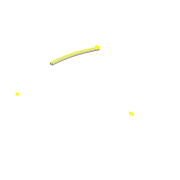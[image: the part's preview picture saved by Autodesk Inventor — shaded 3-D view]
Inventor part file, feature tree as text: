
AUTODESK INVENTOR PART (.ipt)
format: ipt  version: 2022 (Build 260153000, 153)  size: 128,512 bytes
history: native  units: mm
features: sketch x4, extrude x2, projected_geometry x2, fillet x1
ambient origin geometry x8: Origin, YZ Plane, XZ Plane, XY Plane, X Axis, Y Axis, Z Axis, Center Point
bodies: Solid1 (feature_tree)
feature tree (9):
  extrude  "Extrusion1"  Depth=10.0mm
  fillet  "Fillet1"  Radius=3.0mm
  sketch  "Sketch2"  dims[d3=3.0mm d4=8.0mm d5=0.0mm]
  extrude  "Extrusion2"  Depth=8.0mm TaperAngle=0.0deg
  sketch  "Sketch4"  dims[d13=400.0mm d14=2.0mm d15=30.0mm d16=180.0mm d17=190.354919mm d18=20.0mm d19=0.0mm]
  sketch  "Sketch1"  dims[d0=382.775mm d1=10.0mm d2=3.0mm]
  projected_geometry  "Projected Loop1"
  sketch  "Sketch3"  dims[d12=400.0mm]
  projected_geometry  "Projected Loop2"
